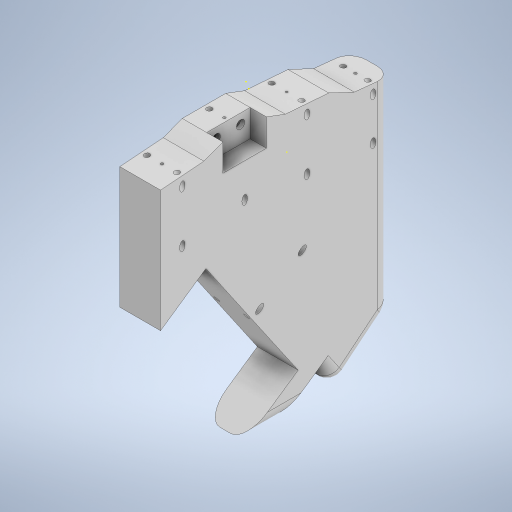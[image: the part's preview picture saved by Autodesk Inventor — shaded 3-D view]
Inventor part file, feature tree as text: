
AUTODESK INVENTOR PART (.ipt)
format: ipt  version: 2024 (Build 280153000, 153)  size: 866,816 bytes
history: native  units: mm
features: sketch x53, extrude x25, move_body x7, sweep x6, fillet x4, split x4, boolean_combine x4, other x1, plane x1
ambient origin geometry x8: Origin, YZ Plane, XZ Plane, XY Plane, X Axis, Y Axis, Z Axis, Center Point
bodies: Solid1 (feature_tree), Solid3 (feature_tree), Solid4 (feature_tree), Solid5 (feature_tree), Solid6 (feature_tree), Solid7 (feature_tree), Solid8 (feature_tree), Solid9 (feature_tree), Solid10 (feature_tree)
feature tree (105):
  other  "Repaired Geometry1"
  extrude  "Extrusion1"  Depth=85.0mm
  extrude  "Extrusion2"  Depth=15.0mm
  extrude  "Extrusion3"  Depth=16.0mm
  extrude  "Extrusion4"  Depth=16.0mm
  extrude  "Extrusion5"  Depth=14.0mm
  fillet  "Fillet1"  Radius=18.25mm
  sketch  "Sketch10"  dims[d14=3.0mm d15=16.0mm]
  fillet  "Fillet2"  Radius=16.0mm
  sketch  "Sketch11"  dims[d16=3.0mm d17=16.0mm]
  sketch  "Sketch12"  dims[d18=180.0deg d19=5.0mm]
  sketch  "Sketch13"  dims[d20=14.0mm d21=4.0mm]
  sketch  "Sketch14"  dims[d22=24.958208mm d23=24.0mm d24=0.0mm]
  extrude  "Extrusion6"  Depth=16.0mm
  sweep  "Sweep5"
  sweep  "Sweep6"
  sweep  "Sweep7"
  sweep  "Sweep8"
  extrude  "Extrusion7"  Depth=70.0mm
  extrude  "Extrusion8"  Depth=10.0mm
  sweep  "Sweep9"
  sketch  "Sketch27"  dims[d51=11.0mm d52=2.0mm]
  extrude  "Extrusion9"  Depth=15.0mm TaperAngle=0.0deg
  extrude  "Extrusion10"  Depth=5.5mm
  plane  "Work Plane1"
  sketch  "Sketch30"  dims[d57=2.0mm d58=14.0mm]
  extrude  "Extrusion11"  Depth=9.0mm
  extrude  "Extrusion12"  Depth=11.0mm
  split  "Split1"
  move_body  "Move Body2"
  sketch  "Sketch34"  dims[d77=60.0deg d78=0.0mm d79=0.0mm]
  extrude  "Extrusion13"  Depth=2.0mm
  split  "Split2"
  move_body  "Move Body3"
  extrude  "Extrusion14"  Depth=15.0mm
  split  "Split3"
  move_body  "Move Body4"
  split  "Split4"
  move_body  "Move Body5"
  extrude  "Extrusion15"  Depth=2.0mm
  move_body  "Move Body6"
  boolean_combine  "Combine1"
  move_body  "Move Body7"
  boolean_combine  "Combine2"
  extrude  "Extrusion16"  Depth=2.0mm
  boolean_combine  "Combine3"
  move_body  "Move Body8"
  boolean_combine  "Combine4"
  extrude  "Extrusion17"  Depth=15.0mm
  sketch  "Sketch44"  dims[d97=0.0mm d98=0.0mm]
  sketch  "Sketch45"  dims[d99=1.0mm]
  extrude  "Extrusion18"  Depth=11.0mm
  extrude  "Extrusion19"  Depth=14.0mm
  sketch  "Sketch48"  dims[d103=10.0mm d104=0.0mm]
  extrude  "Extrusion20"  Depth=1.0mm
  extrude  "Extrusion21"  TaperAngle=60.0deg  [1 undecoded]
  extrude  "Extrusion22"  Depth=40.0mm
  sketch  "Sketch53"  dims[d111=7.5mm d112=5.0mm d113=0.0mm d114=0.0mm]
  extrude  "Extrusion23"  TaperAngle=0.0deg  [1 undecoded]
  sketch  "Sketch55"  dims[d116=16.0mm]
  sketch  "Sketch56"  dims[d117=0.0mm d118=0.0mm d119=20.0mm]
  sweep  "Sweep10"
  sketch  "Sketch63"  dims[d124=0.0mm d125=0.0mm d126=-40.0mm]
  extrude  "Extrusion27"  Depth=40.0mm
  extrude  "Extrusion28"  TaperAngle=0.0deg  [1 undecoded]
  fillet  "Fillet6"  Radius=1.0mm
  fillet  "Fillet7"  Radius=1.0mm
  sketch  "Sketch1"  dims[d0=30.0mm d1=85.0mm]
  sketch  "Sketch2"  dims[d2=15.0mm d3=0.0mm d4=16.0mm]
  sketch  "Sketch3"  dims[d5=3.0mm d6=16.0mm]
  sketch  "Sketch24"  dims[d45=0.0mm d46=2.0mm]
  sketch  "Sketch8"  dims[d7=3.0mm d8=16.0mm]
  sketch  "Sketch9"  dims[d9=5.0mm d10=14.0mm d11=18.25mm d12=0.0mm d13=16.0mm]
  sketch  "Sketch17"  dims[d26=73.0mm d27=70.0mm]
  sketch  "Sketch18"  dims[d28=10.0mm d31=50.0mm]
  sketch  "Sketch19"  dims[d32=60.0mm d33=40.0mm]
  sketch  "Sketch20"  dims[d34=15.0mm d35=0.0mm d36=15.0mm d37=0.0mm]
  sketch  "Sketch21"  dims[d38=5.5mm d39=5.5mm]
  sketch  "Sketch22"  dims[d41=16.0mm d42=9.0mm]
  sketch  "Sketch23"  dims[d43=2.0mm d44=11.0mm]
  sketch  "Sketch25"  dims[d47=15.0mm d48=16.0mm]
  sketch  "Sketch26"  dims[d49=9.0mm d50=2.0mm]
  sketch  "Sketch28"  dims[d53=15.0mm d54=16.0mm]
  sketch  "Sketch29"  dims[d55=2.0mm d56=11.0mm]
  sketch  "Sketch31"  dims[d61=2.0mm d70=1.0mm]
  sketch  "Sketch32"  dims[d71=1.0mm d72=0.0mm d73=60.0deg]
  sketch  "Sketch33"  dims[d74=0.0mm d75=0.0mm d76=40.0mm]
  sketch  "Sketch35"  dims[d80=40.0mm d81=60.0deg]
  sketch  "Sketch36"  dims[d82=0.0mm d83=0.0mm d84=40.0mm]
  sketch  "Sketch37"  dims[d85=60.0deg d86=0.0mm d87=0.0mm d88=1.0mm d89=1.0mm d90=0.0mm]
  sketch  "Sketch38"  dims[d91=1.0mm d92=0.0mm]
  sketch  "Sketch39"  dims[d93=9.0mm]
  sketch  "Sketch40"  dims[d94=2.0mm]
  sketch  "Sketch41"  dims[d95=40.0mm]
  sketch  "Sketch43"  dims[d96=60.0deg]
  sketch  "Sketch46"  dims[d100=1.0mm d101=0.0mm]
  sketch  "Sketch47"  dims[d102=6.0mm]
  sketch  "Sketch50"  dims[d105=-1.5mm]
  sketch  "Sketch51"  dims[d108=2.5mm d109=0.0mm]
  sketch  "Sketch52"  dims[d110=3.1mm]
  sketch  "Sketch54"  dims[d115=30.0mm]
  sketch  "Sketch57"  dims[d120=7.0mm]
  sketch  "Sketch58"  dims[d122=15.0mm d123=0.0mm]
  sketch  "Sketch64"  dims[d127=3.612832mm]
  sketch  "Sketch65"  dims[d128=15.0mm d129=0.0mm d130=0.0mm d131=0.0mm d132=36.0mm d133=20.0mm d134=0.0mm d135=0.0mm d136=-30.0mm d137=15.0mm d138=0.0mm d139=0.0mm d140=0.0mm d141=10.0mm d142=0.0mm d143=0.0mm d144=21.64mm d145=9.0mm d146=0.0mm d147=0.0mm d148=0.0mm d149=-16.0mm d150=8.25mm d151=0.0mm d155=2.5mm d156=0.0mm d157=3.1mm d158=14.0mm d159=5.0mm d160=0.0mm d161=0.0mm d162=15.0mm d163=0.0mm d164=15.0mm d165=0.0mm d166=15.0mm d167=0.0mm d168=4.0mm d169=0.0mm d170=14.0mm d171=32.0mm d172=2.0mm d173=2.0mm d174=60.0deg d175=0.0mm d176=0.0mm d183=7.0mm d184=24.75mm d185=0.0mm d186=24.75mm d187=0.0mm d188=4.5mm d189=4.5mm d106=0.872665mm d152=0.5mm d153=0.872665mm d154=0.0mm]
note: 3 required parameter values undecoded (feature->parameter linkage not recoverable at this tier; creation-order binding heuristic only, values carry confidence <= 0.55)
